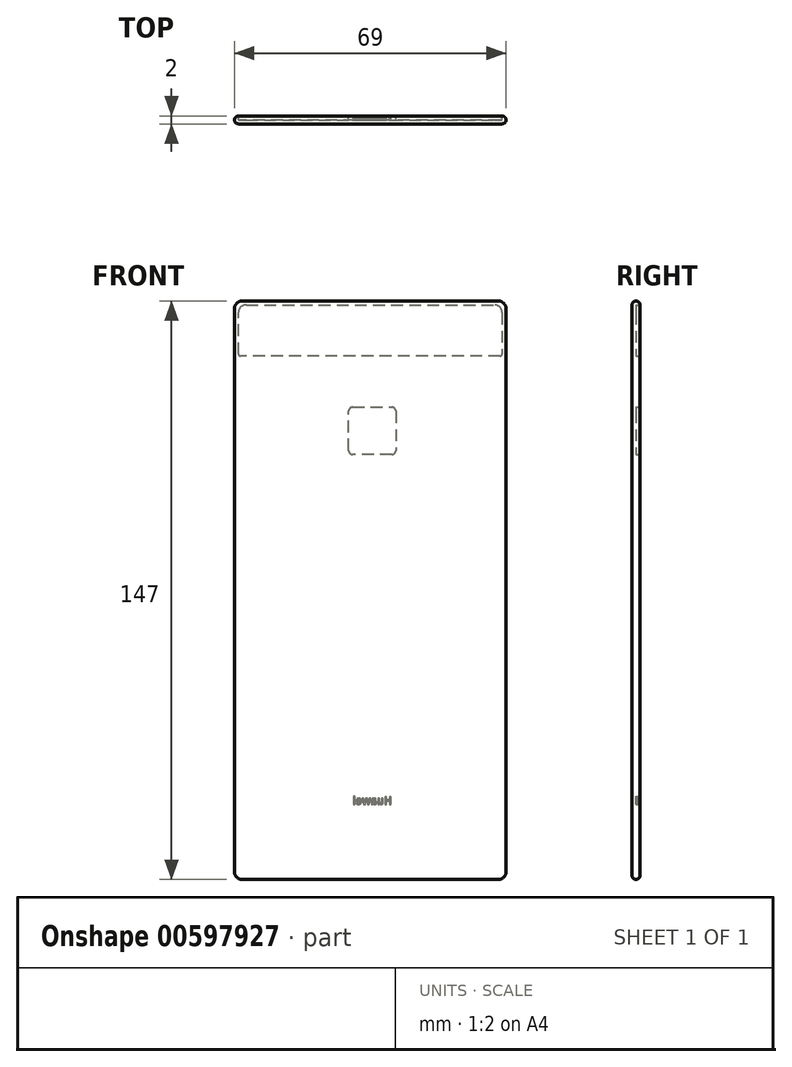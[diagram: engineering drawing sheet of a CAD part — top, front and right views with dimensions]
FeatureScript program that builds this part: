
annotation { "Feature Type Name" : "Feature", "Feature Type Description" : "" }
export const myFeature = defineFeature(function(context is Context, id is Id, definition is map)
    precondition{}
    {
        {
            var Q0;
            Q0=qCreatedBy(makeId("Front.planeOp"),FACE);
            var sketch = newSketch(context, id + "F0", { "sketchPlane" : qUnion([Q0])});
            skLineSegment(sketch, "E0", {"start": v(-2, 0) * mm, "end": v(-67, 0) * mm});
            skLineSegment(sketch, "E1", {"start": v(-69, 2) * mm, "end": v(-69, 145) * mm});
            skLineSegment(sketch, "E2", {"start": v(-67, 147) * mm, "end": v(-2, 147) * mm});
            skLineSegment(sketch, "E3", {"start": v(0, 145) * mm, "end": v(0, 2) * mm});
            skPoint(sketch, "E4.visualSharp", {"position": v(0, 0) * mm});
            skArc(sketch, "E4.filletArc", {"start": v(-2, 0) * mm, "mid": v(-0.59, 0.59) * mm, "end": v(0, 2) * mm});
            skPoint(sketch, "E5.visualSharp", {"position": v(-69, 0) * mm});
            skArc(sketch, "E5.filletArc", {"start": v(-69, 2) * mm, "mid": v(-68.41, 0.59) * mm, "end": v(-67, 0) * mm});
            skPoint(sketch, "E6.visualSharp", {"position": v(-69, 147) * mm});
            skArc(sketch, "E6.filletArc", {"start": v(-67, 147) * mm, "mid": v(-68.41, 146.41) * mm, "end": v(-69, 145) * mm});
            skPoint(sketch, "E7.visualSharp", {"position": v(0, 147) * mm});
            skArc(sketch, "E7.filletArc", {"start": v(0, 145) * mm, "mid": v(-0.59, 146.41) * mm, "end": v(-2, 147) * mm});
            skSolve(sketch);
        }
        {
            var Q0;
            Q0=makeQuery(id+"F0.imprint","IMPRINT",FACE,{"disambiguationData":[TD([[makeQuery(id+"F0.imprint","IMPRINT",EDGE,{"derivedFrom":sQuery(id+"F0.wireOp",EDGE,"E0")}),-1.0]])]});
            extrude(context, id + "F1", {"entities" : qUnion([Q0]), "oppositeDirection" : true, "depth" : 2 * mm, "offsetDistance" : 25 * mm});
        }
        {
            var Q0;
            Q0=makeQuery(id+"F1.opExtrude","CAP_FACE",FACE,{"disambiguationData":[OSD([sQuery(id+"F0.wireOp",EDGE,"E0"),sQuery(id+"F0.wireOp",EDGE,"E1"),sQuery(id+"F0.wireOp",EDGE,"E2"),sQuery(id+"F0.wireOp",EDGE,"E3"),sQuery(id+"F0.wireOp",EDGE,"E4.filletArc"),sQuery(id+"F0.wireOp",EDGE,"E5.filletArc"),sQuery(id+"F0.wireOp",EDGE,"E6.filletArc"),sQuery(id+"F0.wireOp",EDGE,"E7.filletArc")])],"isStart":false});
            var sketch = newSketch(context, id + "F2", { "sketchPlane" : qUnion([Q0])});
            skLineSegment(sketch, "E8", {"start": v(1.5, 133) * mm, "end": v(67.5, 133) * mm});
            skLineSegment(sketch, "E9", {"start": v(68, 133.5) * mm, "end": v(68, 144) * mm});
            skLineSegment(sketch, "E10", {"start": v(66, 146) * mm, "end": v(3, 146) * mm});
            skLineSegment(sketch, "E11", {"start": v(1, 144) * mm, "end": v(1, 133.5) * mm});
            skPoint(sketch, "E12.visualSharp", {"position": v(1, 146) * mm});
            skArc(sketch, "E12.filletArc", {"start": v(3, 146) * mm, "mid": v(1.59, 145.41) * mm, "end": v(1, 144) * mm});
            skPoint(sketch, "E13.visualSharp", {"position": v(68, 146) * mm});
            skArc(sketch, "E13.filletArc", {"start": v(68, 144) * mm, "mid": v(67.41, 145.41) * mm, "end": v(66, 146) * mm});
            skPoint(sketch, "E14.visualSharp", {"position": v(1, 133) * mm});
            skArc(sketch, "E14.filletArc", {"start": v(1, 133.5) * mm, "mid": v(1.15, 133.15) * mm, "end": v(1.5, 133) * mm});
            skPoint(sketch, "E15.visualSharp", {"position": v(68, 133) * mm});
            skArc(sketch, "E15.filletArc", {"start": v(67.5, 133) * mm, "mid": v(67.85, 133.15) * mm, "end": v(68, 133.5) * mm});
            skSolve(sketch);
        }
        {
            var Q0;
            Q0=makeQuery(id+"F2.imprint","IMPRINT",FACE,{"disambiguationData":[TD([[makeQuery(id+"F2.imprint","IMPRINT",EDGE,{"derivedFrom":sQuery(id+"F2.wireOp",EDGE,"E8")}),1.0]])]});
            extrude(context, id + "F3", {"entities" : qUnion([Q0]), "operationType" : NewBodyOperationType.REMOVE, "oppositeDirection" : true, "depth" : 1 * mm, "offsetDistance" : 25 * mm});
        }
        {
            var Q0;
            Q0=makeQuery(id+"F1.opExtrude","CAP_FACE",FACE,{"disambiguationData":[OSD([sQuery(id+"F0.wireOp",EDGE,"E0"),sQuery(id+"F0.wireOp",EDGE,"E1"),sQuery(id+"F0.wireOp",EDGE,"E2"),sQuery(id+"F0.wireOp",EDGE,"E3"),sQuery(id+"F0.wireOp",EDGE,"E4.filletArc"),sQuery(id+"F0.wireOp",EDGE,"E5.filletArc"),sQuery(id+"F0.wireOp",EDGE,"E6.filletArc"),sQuery(id+"F0.wireOp",EDGE,"E7.filletArc")])],"isStart":false});
            var sketch = newSketch(context, id + "F4", { "sketchPlane" : qUnion([Q0])});
            skLineSegment(sketch, "E16", {"start": v(28, 119) * mm, "end": v(28, 109) * mm});
            skLineSegment(sketch, "E17", {"start": v(29, 108) * mm, "end": v(39, 108) * mm});
            skLineSegment(sketch, "E18", {"start": v(40, 109) * mm, "end": v(40, 119) * mm});
            skLineSegment(sketch, "E19", {"start": v(39, 120) * mm, "end": v(29, 120) * mm});
            skText(sketch, "E20", { "text": "Huawei", "fontName": "OpenSans-Bold.ttf"});
            skPoint(sketch, "E21.visualSharp", {"position": v(40, 120) * mm});
            skArc(sketch, "E21.filletArc", {"start": v(40, 119) * mm, "mid": v(39.7, 119.7) * mm, "end": v(39, 120) * mm});
            skPoint(sketch, "E22.visualSharp", {"position": v(28, 120) * mm});
            skArc(sketch, "E22.filletArc", {"start": v(29, 120) * mm, "mid": v(28.3, 119.7) * mm, "end": v(28, 119) * mm});
            skPoint(sketch, "E23.visualSharp", {"position": v(28, 108) * mm});
            skArc(sketch, "E23.filletArc", {"start": v(28, 109) * mm, "mid": v(28.3, 108.3) * mm, "end": v(29, 108) * mm});
            skPoint(sketch, "E24.visualSharp", {"position": v(40, 108) * mm});
            skArc(sketch, "E24.filletArc", {"start": v(39, 108) * mm, "mid": v(39.7, 108.3) * mm, "end": v(40, 109) * mm});
            const initialGuessF4  = {"E20": [0.029, 0.01915, 1, 0, 0.0019]};
            skSetInitialGuess(sketch, initialGuessF4);
            skSolve(sketch);
        }
        {
            var Q0;
            Q0=makeQuery(id+"F1.opExtrude","CAP_EDGE",EDGE,{"disambiguationData":[OSD([sQuery(id+"F0.wireOp",EDGE,"E7.filletArc")])],"isStart":false});
            var Q1;
            Q1=makeQuery(id+"F1.opExtrude","CAP_EDGE",EDGE,{"disambiguationData":[OSD([sQuery(id+"F0.wireOp",EDGE,"E6.filletArc")])],"isStart":true});
            var Q2;
            Q2=makeQuery(id+"F1.opExtrude","CAP_EDGE",EDGE,{"disambiguationData":[OSD([sQuery(id+"F0.wireOp",EDGE,"E4.filletArc")])],"isStart":false});
            var Q3;
            Q3=makeQuery(id+"F1.opExtrude","CAP_EDGE",EDGE,{"disambiguationData":[OSD([sQuery(id+"F0.wireOp",EDGE,"E5.filletArc")])],"isStart":false});
            fillet(context, id + "F5", {"entities" : qUnion([Q0, Q1, Q2, Q3]), "radius" : 1 * mm, "tangentPropagation" : true, "allowEdgeOverflow" : false});
        }
        {
            var Q0;
            Q0 = qSketchRegion(id + "F4", true);
            extrude(context, id + "F6", {"entities" : qUnion([Q0]), "operationType" : NewBodyOperationType.REMOVE, "oppositeDirection" : true, "depth" : 1 * mm, "offsetDistance" : 25 * mm});
        }
    });
